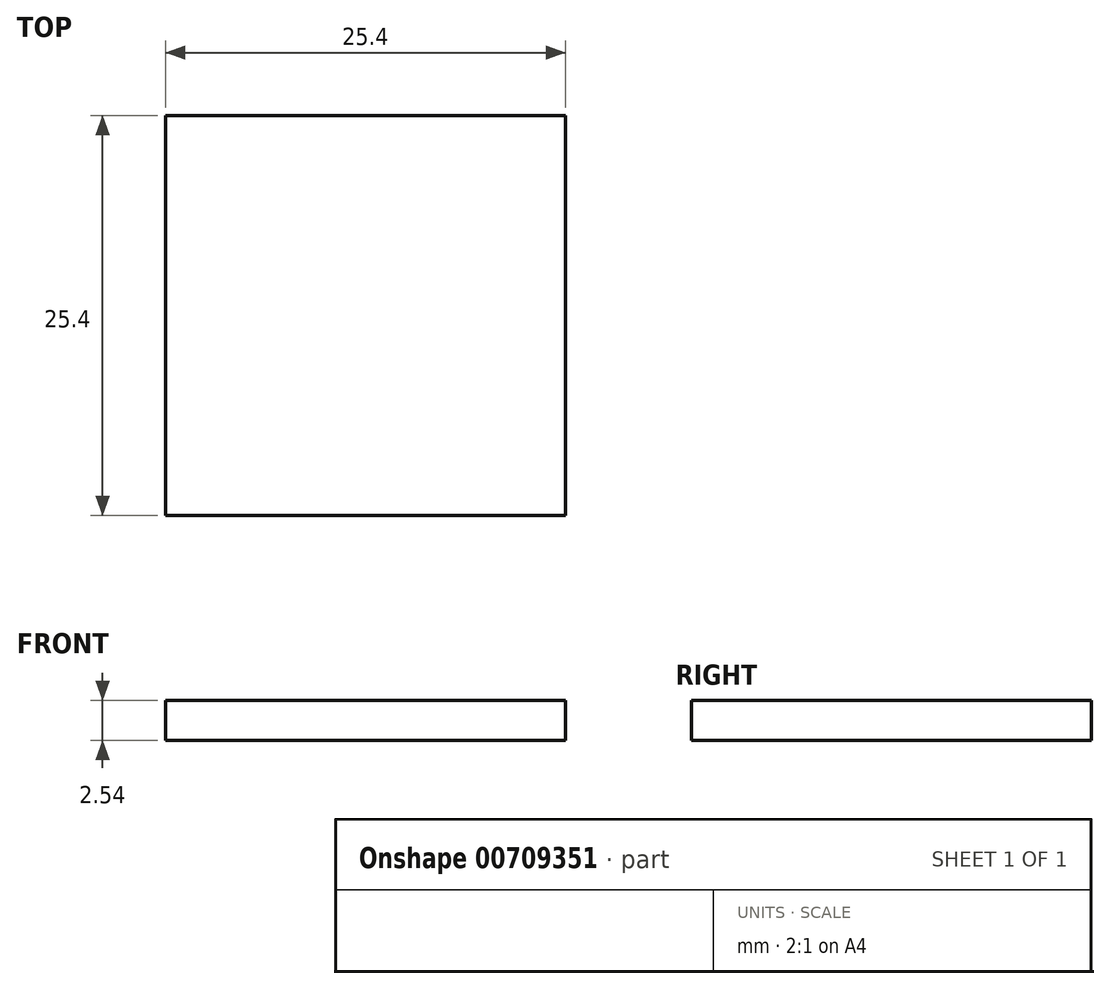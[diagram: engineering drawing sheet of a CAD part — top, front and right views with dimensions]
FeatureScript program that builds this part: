
annotation { "Feature Type Name" : "Feature", "Feature Type Description" : "" }
export const myFeature = defineFeature(function(context is Context, id is Id, definition is map)
    precondition{}
    {
        {
            var Q0;
            Q0=qCreatedBy(makeId("Top.planeOp"),FACE);
            cPlane(context, id + "F0", {"entities" : qUnion([Q0]), "cplaneType" : CPlaneType.OFFSET, "offset" : 25.4 * mm, "width" : 152.4 * mm, "height" : 152.4 * mm});
        }
        {
            var Q0;
            Q0=qCreatedBy(id+"F0.planeOp",FACE);
            var sketch = newSketch(context, id + "F1", { "sketchPlane" : qUnion([Q0])});
            skLineSegment(sketch, "E0.bottom", {"start": v(-5.57, -11.74) * mm, "end": v(19.83, -11.74) * mm});
            skLineSegment(sketch, "E0.top", {"start": v(-5.57, 13.66) * mm, "end": v(19.83, 13.66) * mm});
            skLineSegment(sketch, "E0.left", {"start": v(-5.57, -11.74) * mm, "end": v(-5.57, 13.66) * mm});
            skLineSegment(sketch, "E0.right", {"start": v(19.83, -11.74) * mm, "end": v(19.83, 13.66) * mm});
            skSolve(sketch);
        }
        {
            var Q0;
            Q0=makeQuery(id+"F1.imprint","IMPRINT",FACE,{"disambiguationData":[TD([[makeQuery(id+"F1.imprint","IMPRINT",EDGE,{"derivedFrom":sQuery(id+"F1.wireOp",EDGE,"E0.bottom")}),1.0]])]});
            extrude(context, id + "F2", {"entities" : qUnion([Q0]), "oppositeDirection" : true, "depth" : 2.54 * mm, "offsetDistance" : 25.4 * mm});
        }
        {
            var Q0;
            Q0=makeQuery(id+"F2.opExtrude","CAP_FACE",FACE,{"disambiguationData":[OSD([sQuery(id+"F1.wireOp",EDGE,"E0.bottom"),sQuery(id+"F1.wireOp",EDGE,"E0.top"),sQuery(id+"F1.wireOp",EDGE,"E0.left"),sQuery(id+"F1.wireOp",EDGE,"E0.right")])],"isStart":false});
            var sketch = newSketch(context, id + "F3", { "sketchPlane" : qUnion([Q0])});
            skCircle(sketch, "E1", {"center": v(7.13, -0.96) * mm, "radius": 12.38 * mm});
            skPoint(sketch, "E1.centerSnap0", {"position": v(7.13, -13.66) * mm});
            skPoint(sketch, "E1.centerSnap1", {"position": v(19.83, -0.96) * mm});
            skSolve(sketch);
        }
    });
